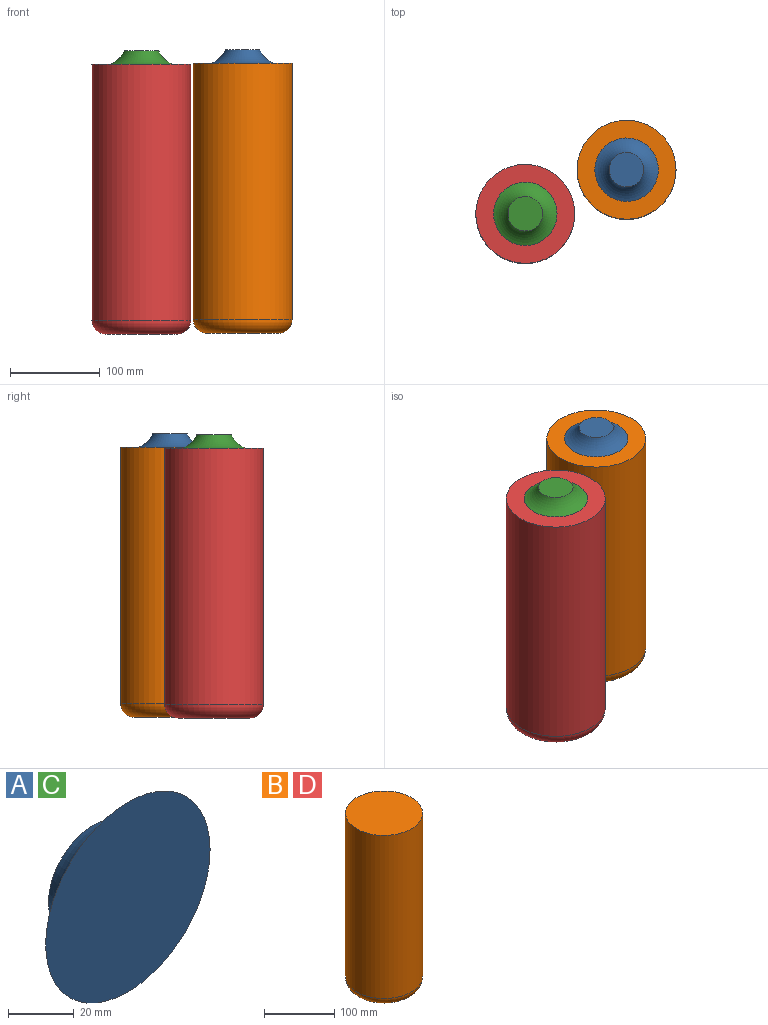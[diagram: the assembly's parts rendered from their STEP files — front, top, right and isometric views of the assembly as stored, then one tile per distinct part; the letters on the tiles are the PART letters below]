
ASSEMBLY  parts=4 mates=2
PART A: 3 faces, bbox 97.7x28.5x97.7 mm
  f0: plane 38.34x38.34mm, normal (0,1,0), area 1154.3mm2, adj f1
  f1: torus R=45.15mm, axis (0,-1,0), area 3729.1mm2, adj f0,f2
  f2: plane 70.62x70.62mm, normal (0,-1,0), area 3916.4mm2, adj f1
PART B: 4 faces, bbox 119.1x119.1x300 mm
  f0: cylinder r=55mm len=285mm, axis (0,0,1), area 98488.9mm2, adj f1,f3
  f1: plane 110x110mm, normal (0,0,1), area 9503.3mm2, adj f0
  f2: plane 80x80mm, normal (0,0,-1), area 5026.5mm2, adj f3
  f3: torus R=40mm, axis (0,0,1), area 7335.5mm2, adj f0,f2
PART C: same geometry as A
PART D: same geometry as B
PLACE A rot(axis=(1,0,0),90deg) t=(69.59,31.67,150)mm
PLACE B t=(69.59,31.67,-150)mm
PLACE C rot(axis=(1,0,0),90deg) t=(-43.06,-17.39,149.05)mm
PLACE D t=(-43.06,-17.39,-150.95)mm
MATE fastened A.f1 <-> B.f0  axis (0,0,-1) through (69.59,31.67,150)mm
MATE fastened C.f1 <-> D.f0  axis (0,0,-1) through (-43.06,-17.39,149.05)mm
